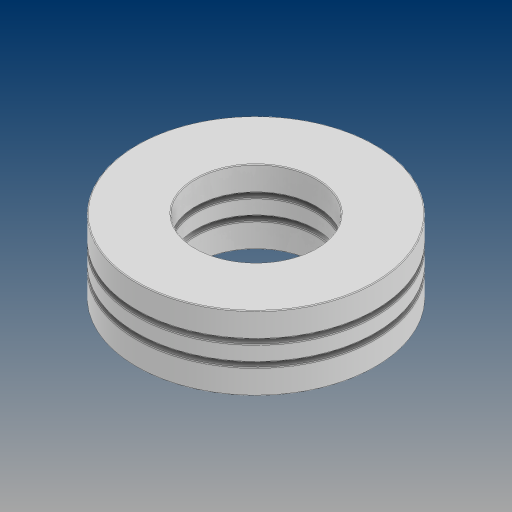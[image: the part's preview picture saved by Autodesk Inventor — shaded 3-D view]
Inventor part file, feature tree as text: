
AUTODESK INVENTOR PART (.ipt)
format: ipt  version: 2024.3 (Build 283343000, 343)  size: 334,336 bytes
history: native  units: in
note: dims shown in document units (in); Inventor stores cm internally (conversion verified against a paired STEP export)
features: fillet x3, other x2, revolve x1
ambient origin geometry x8: Origin, YZ Plane, XZ Plane, XY Plane, X Axis, Y Axis, Z Axis, Center Point
bodies: Solid1 (feature_tree), Solid2 (feature_tree), Solid3 (feature_tree), Solid4 (feature_tree), Solid5 (feature_tree), Solid6 (feature_tree)
feature tree (6):
  revolve  "Revolve2"  [1 undecoded]
  other  "CirPattern1[1]"
  other  "CirPattern1[2]"
  fillet  "Fillet2"  [1 undecoded]
  fillet  "Fillet1"  [1 undecoded]
  fillet  "Fillet3"  [1 undecoded]
note: 4 required parameter values undecoded (feature->parameter linkage not recoverable at this tier; creation-order binding heuristic only, values carry confidence <= 0.55)
